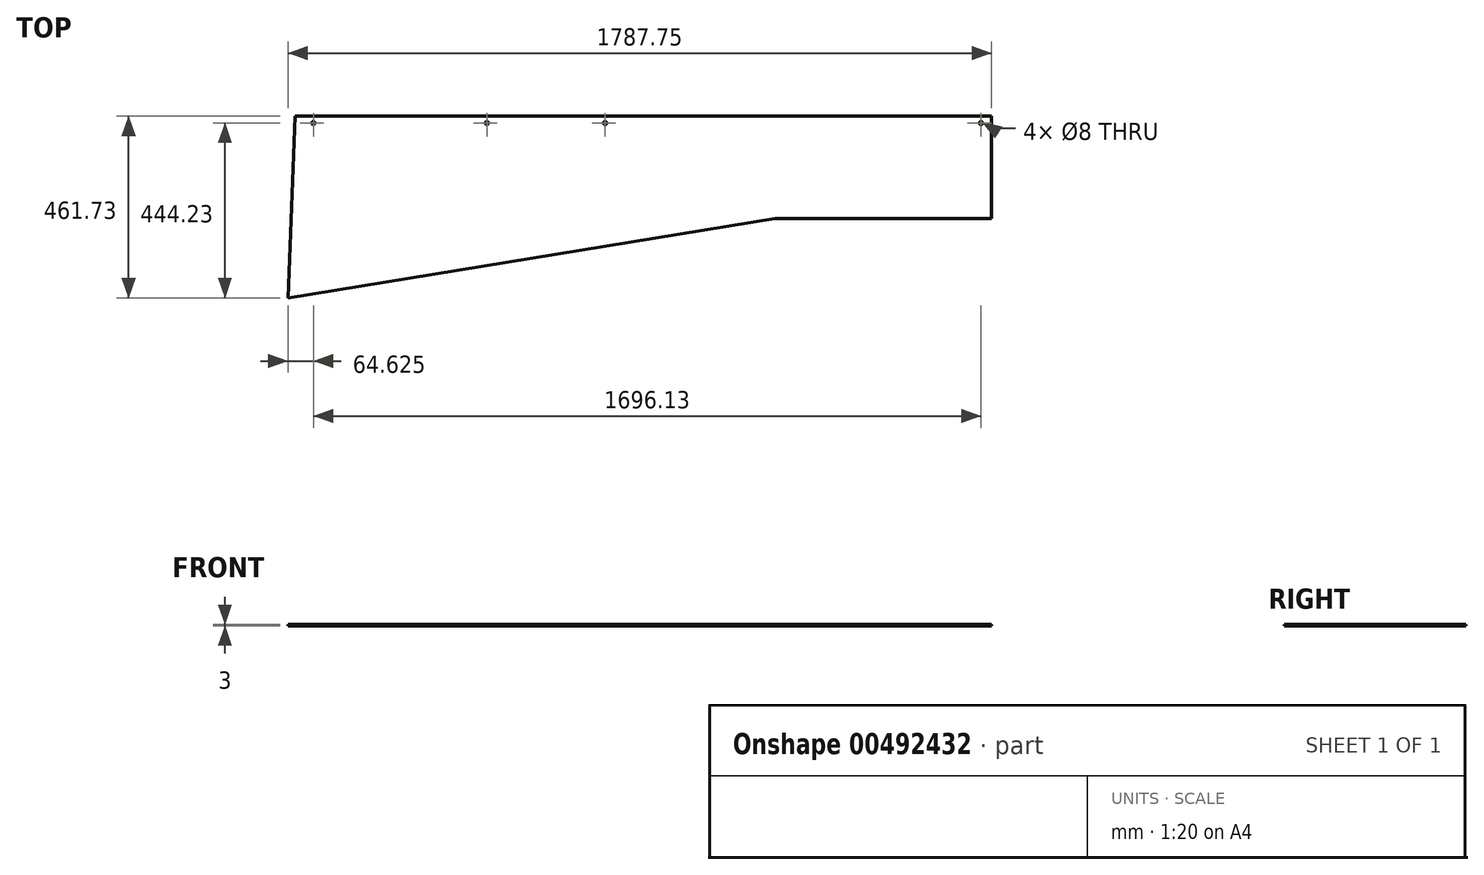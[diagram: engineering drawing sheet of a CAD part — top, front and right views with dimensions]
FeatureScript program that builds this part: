
annotation { "Feature Type Name" : "Feature", "Feature Type Description" : "" }
export const myFeature = defineFeature(function(context is Context, id is Id, definition is map)
    precondition{}
    {
        {
            var Q0;
            Q0=qCreatedBy(makeId("Top.planeOp"),FACE);
            var sketch = newSketch(context, id + "F0", { "sketchPlane" : qUnion([Q0])});
            skLineSegment(sketch, "E0", {"start": v(417.8, -260) * mm, "end": v(967.8, -260) * mm});
            skLineSegment(sketch, "E1", {"start": v(967.8, -260) * mm, "end": v(967.8, 0) * mm});
            skLineSegment(sketch, "E2", {"start": v(967.8, 0) * mm, "end": v(-802.2, 0) * mm});
            skLineSegment(sketch, "E3", {"start": v(-802.2, 0) * mm, "end": v(-812.2, -260) * mm});
            skLineSegment(sketch, "E4", {"start": v(-802.2, 0) * mm, "end": v(-819.95, -461.73) * mm});
            skLineSegment(sketch, "E5", {"start": v(-819.95, -461.73) * mm, "end": v(417.8, -260) * mm});
            skCircle(sketch, "E6", {"center": v(940.8, -17.5) * mm, "radius": 4 * mm});
            skCircle(sketch, "E7", {"center": v(-13.97, -17.5) * mm, "radius": 4 * mm});
            skCircle(sketch, "E8", {"center": v(-314.52, -17.5) * mm, "radius": 4 * mm});
            skCircle(sketch, "E9", {"center": v(-755.33, -17.5) * mm, "radius": 4 * mm});
            skSolve(sketch);
        }
        {
            var Q0;
            Q0=makeQuery(id+"F0.imprint","IMPRINT",FACE,{"disambiguationData":[TD([[makeQuery(id+"F0.imprint","IMPRINT",EDGE,{"derivedFrom":sQuery(id+"F0.wireOp",EDGE,"E0")}),1.0]])]});
            extrude(context, id + "F1", {"entities" : qUnion([Q0]), "flatOperationType" : FlatOperationType.REMOVE, "offsetDistance" : 25 * mm, "depth" : 3 * mm, "domain" : OperationDomain.MODEL});
        }
    });
